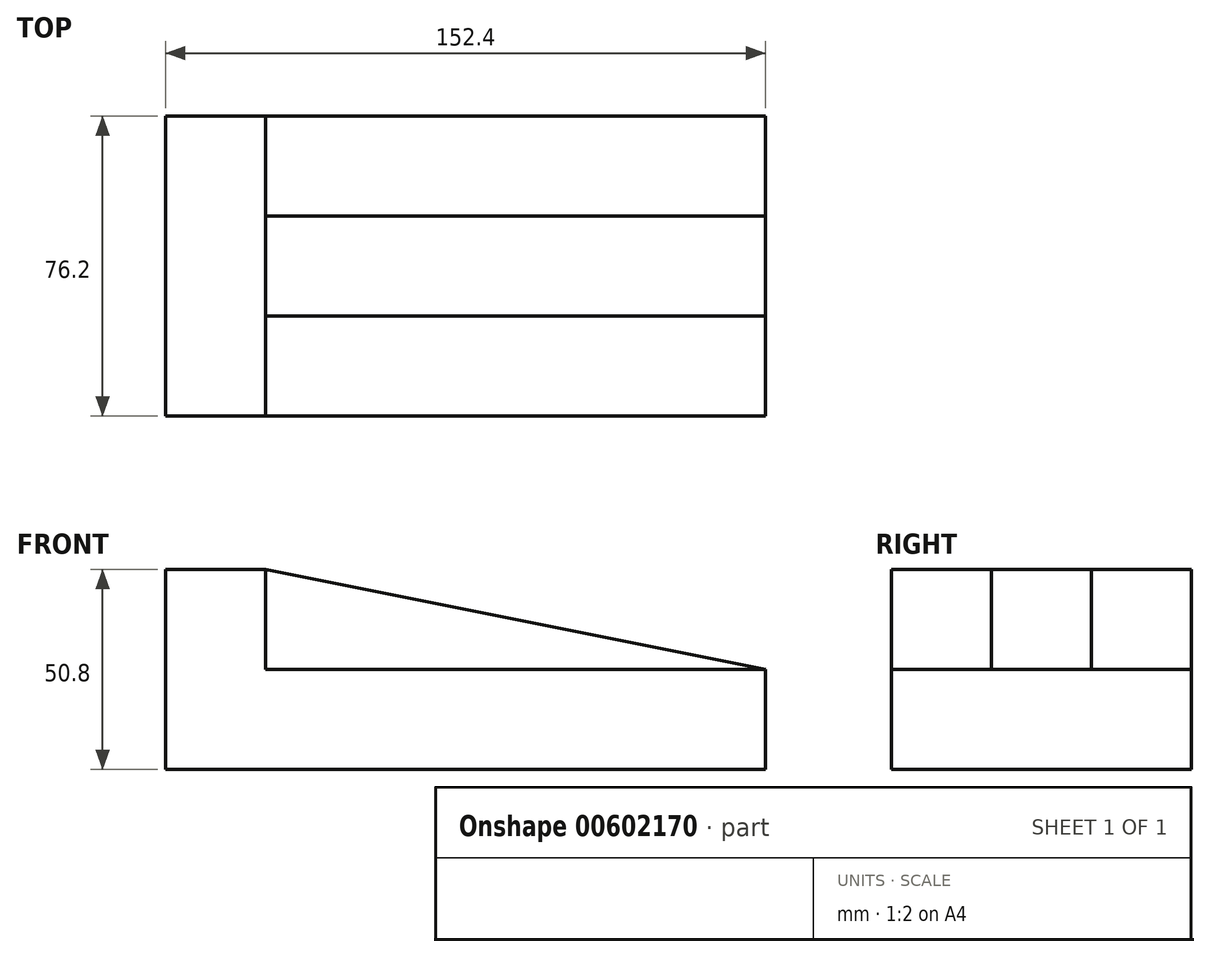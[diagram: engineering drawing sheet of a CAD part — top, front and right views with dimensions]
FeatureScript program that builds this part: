
annotation { "Feature Type Name" : "Feature", "Feature Type Description" : "" }
export const myFeature = defineFeature(function(context is Context, id is Id, definition is map)
    precondition{}
    {
        {
            var Q0;
            Q0=qCreatedBy(makeId("Front.planeOp"),FACE);
            var sketch = newSketch(context, id + "F0", { "sketchPlane" : qUnion([Q0])});
            skLineSegment(sketch, "E0.bottom", {"start": v(0, 0) * mm, "end": v(152.4, 0) * mm});
            skLineSegment(sketch, "E0.top", {"start": v(0, 50.8) * mm, "end": v(152.4, 50.8) * mm});
            skLineSegment(sketch, "E0.left", {"start": v(0, 0) * mm, "end": v(0, 50.8) * mm});
            skLineSegment(sketch, "E0.right", {"start": v(152.4, 0) * mm, "end": v(152.4, 50.8) * mm});
            skSolve(sketch);
        }
        {
            var Q0;
            Q0 = qSketchRegion(id + "F0", true);
            extrude(context, id + "F1", {"entities" : qUnion([Q0]), "depth" : 76.2 * mm, "offsetDistance" : 25.4 * mm});
        }
        {
            var Q0;
            Q0=makeQuery(id+"F1.opExtrude","SWEPT_FACE",FACE,{"disambiguationData":[OSD([sQuery(id+"F0.wireOp",EDGE,"E0.right")])]});
            var sketch = newSketch(context, id + "F2", { "sketchPlane" : qUnion([Q0])});
            skLineSegment(sketch, "E1.bottom", {"start": v(-76.2, 50.8) * mm, "end": v(-50.8, 50.8) * mm});
            skLineSegment(sketch, "E1.top", {"start": v(-76.2, 25.4) * mm, "end": v(-50.8, 25.4) * mm});
            skLineSegment(sketch, "E1.left", {"start": v(-76.2, 50.8) * mm, "end": v(-76.2, 25.4) * mm});
            skLineSegment(sketch, "E1.right", {"start": v(-50.8, 50.8) * mm, "end": v(-50.8, 25.4) * mm});
            skLineSegment(sketch, "E2.bottom", {"start": v(0, 50.8) * mm, "end": v(-25.4, 50.8) * mm});
            skLineSegment(sketch, "E2.top", {"start": v(0, 25.4) * mm, "end": v(-25.4, 25.4) * mm});
            skLineSegment(sketch, "E2.left", {"start": v(0, 50.8) * mm, "end": v(0, 25.4) * mm});
            skLineSegment(sketch, "E2.right", {"start": v(-25.4, 50.8) * mm, "end": v(-25.4, 25.4) * mm});
            skSolve(sketch);
        }
        {
            var Q0;
            Q0=makeQuery(id+"F2.imprint","IMPRINT",FACE,{"disambiguationData":[TD([[makeQuery(id+"F2.imprint","IMPRINT",EDGE,{"derivedFrom":sQuery(id+"F2.wireOp",EDGE,"E1.bottom")}),-1.0]])]});
            var Q1;
            Q1=makeQuery(id+"F2.imprint","IMPRINT",FACE,{"disambiguationData":[TD([[makeQuery(id+"F2.imprint","IMPRINT",EDGE,{"derivedFrom":sQuery(id+"F2.wireOp",EDGE,"E2.bottom")}),-1.0]])]});
            extrude(context, id + "F3", {"entities" : qUnion([Q0, Q1]), "operationType" : NewBodyOperationType.REMOVE, "oppositeDirection" : true, "depth" : 127 * mm, "offsetDistance" : 25.4 * mm});
        }
        {
            var Q0;
            Q0=makeQuery(id+"F3.boolean.opBoolean","COPY",FACE,{"derivedFrom":makeQuery(id+"F3.opExtrude","SWEPT_FACE",FACE,{"disambiguationData":[OSD([sQuery(id+"F2.wireOp",EDGE,"E1.right")])]})});
            var sketch = newSketch(context, id + "F4", { "sketchPlane" : qUnion([Q0])});
            skLineSegment(sketch, "E3", {"start": v(152.4, 50.8) * mm, "end": v(25.4, 50.8) * mm});
            skLineSegment(sketch, "E4", {"start": v(25.4, 50.8) * mm, "end": v(152.4, 25.4) * mm});
            skLineSegment(sketch, "E5", {"start": v(152.4, 25.4) * mm, "end": v(152.4, 50.8) * mm});
            skSolve(sketch);
        }
        {
            var Q0;
            Q0=makeQuery(id+"F4.imprint","IMPRINT",FACE,{"disambiguationData":[TD([[makeQuery(id+"F4.imprint","IMPRINT",EDGE,{"derivedFrom":sQuery(id+"F4.wireOp",EDGE,"E3")}),-1.0]])]});
            extrude(context, id + "F5", {"entities" : qUnion([Q0]), "operationType" : NewBodyOperationType.REMOVE, "oppositeDirection" : true, "depth" : 76.2 * mm, "offsetDistance" : 25.4 * mm});
        }
    });
